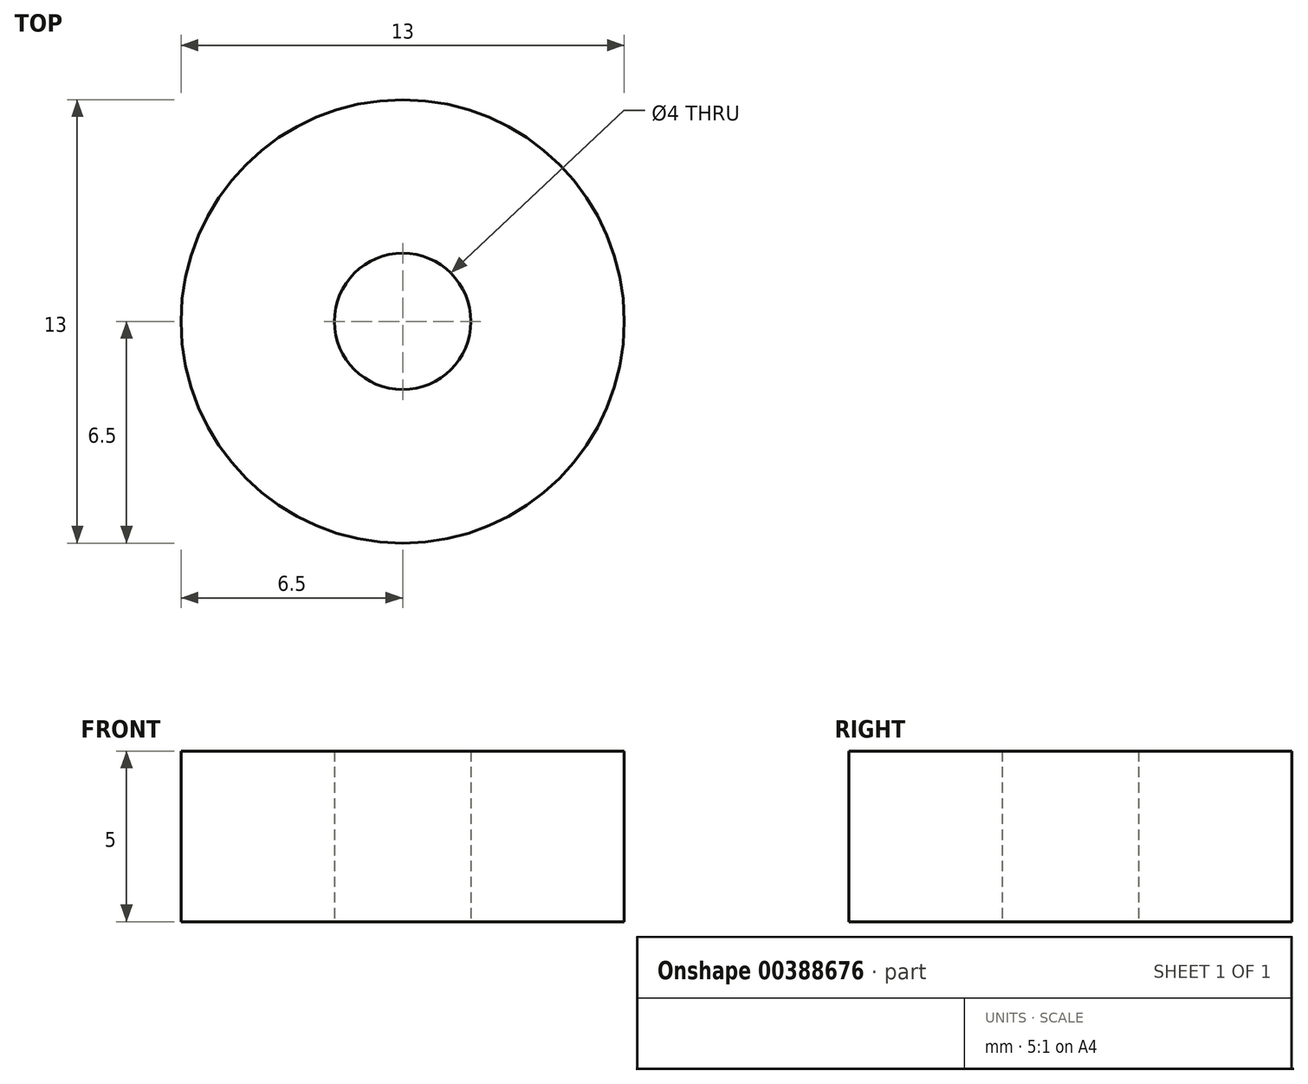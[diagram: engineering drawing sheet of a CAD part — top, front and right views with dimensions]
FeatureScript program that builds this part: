
annotation { "Feature Type Name" : "Feature", "Feature Type Description" : "" }
export const myFeature = defineFeature(function(context is Context, id is Id, definition is map)
    precondition{}
    {
        {
            var Q0;
            Q0=qCreatedBy(makeId("Top.planeOp"),FACE);
            var sketch = newSketch(context, id + "F0", { "sketchPlane" : qUnion([Q0])});
            skCircle(sketch, "E0", {"center": v(0, 0) * mm, "radius": 6.5 * mm});
            skCircle(sketch, "E1", {"center": v(0, 0) * mm, "radius": 2 * mm});
            skSolve(sketch);
        }
        {
            var Q0;
            Q0 = qSketchRegion(id + "F0", true);
            extrude(context, id + "F1", {"entities" : qUnion([Q0]), "depth" : 5 * mm});
        }
    });
